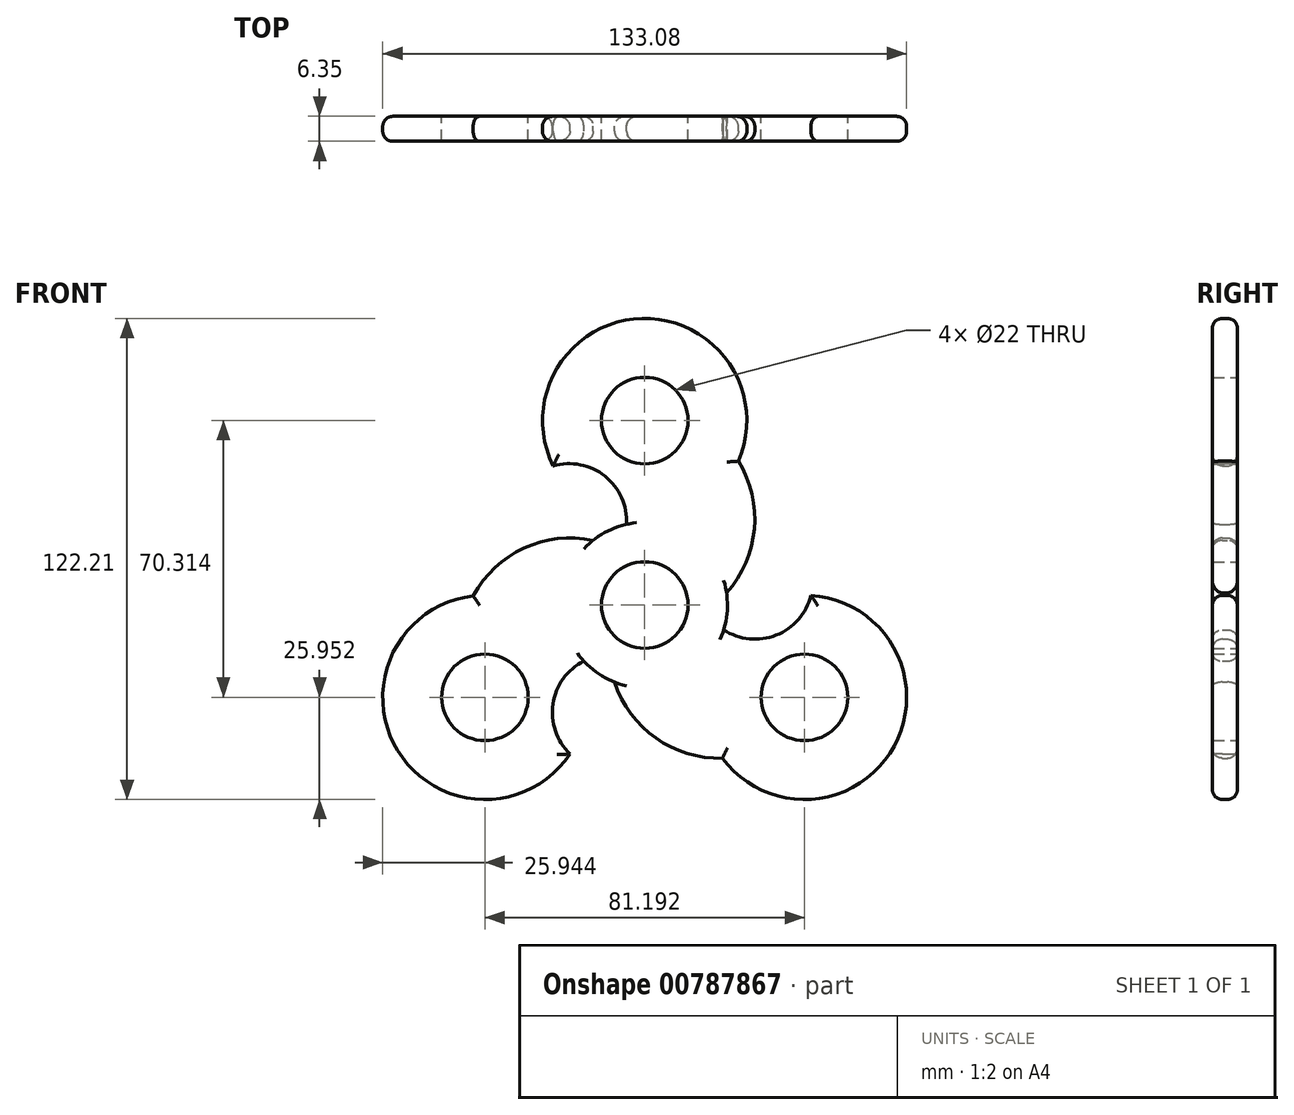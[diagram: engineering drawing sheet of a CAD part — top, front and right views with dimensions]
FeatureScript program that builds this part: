
annotation { "Feature Type Name" : "Feature", "Feature Type Description" : "" }
export const myFeature = defineFeature(function(context is Context, id is Id, definition is map)
    precondition{}
    {
        {
            var Q0;
            Q0=qCreatedBy(makeId("Front.planeOp"),FACE);
            var sketch = newSketch(context, id + "F0", { "sketchPlane" : qUnion([Q0])});
            skCircle(sketch, "E0", {"center": v(0, 0) * mm, "radius": 11 * mm});
            skCircle(sketch, "E1", {"center": v(0, 46.88) * mm, "radius": 11 * mm});
            skArc(sketch, "E2", {"start": v(-15.47, -14.24) * mm, "mid": v(-11.88, -17.34) * mm, "end": v(-7.69, -19.56) * mm});
            skArc(sketch, "E3", {"start": v(20.79, 3.12) * mm, "mid": v(27.85, 19.34) * mm, "end": v(23.81, 36.56) * mm});
            skArc(sketch, "E4", {"start": v(-4.6, 20.51) * mm, "mid": v(-10.08, 32.75) * mm, "end": v(-23.24, 35.33) * mm});
            skArc(sketch, "E5.trimOffspring", {"start": v(23.81, 36.56) * mm, "mid": v(-0.68, 72.82) * mm, "end": v(-23.24, 35.33) * mm});
            skCircle(sketch, "E6.1.0", {"center": v(-40.6, -23.44) * mm, "radius": 11 * mm});
            skArc(sketch, "E6.1.1", {"start": v(-13.1, 16.44) * mm, "mid": v(-30.67, 14.45) * mm, "end": v(-43.57, 2.34) * mm});
            skArc(sketch, "E6.1.2", {"start": v(-43.57, 2.34) * mm, "mid": v(-62.72, -37) * mm, "end": v(-18.98, -37.8) * mm});
            skArc(sketch, "E6.1.3", {"start": v(-15.47, -14.24) * mm, "mid": v(-23.32, -25.1) * mm, "end": v(-18.98, -37.8) * mm});
            skArc(sketch, "E6.1.4", {"start": v(20.06, -6.28) * mm, "mid": v(20.96, -1.62) * mm, "end": v(20.79, 3.12) * mm});
            skCircle(sketch, "E6.2.0", {"center": v(40.6, -23.44) * mm, "radius": 11 * mm});
            skArc(sketch, "E6.2.1", {"start": v(-7.69, -19.56) * mm, "mid": v(2.82, -33.79) * mm, "end": v(19.76, -38.9) * mm});
            skArc(sketch, "E6.2.2", {"start": v(19.76, -38.9) * mm, "mid": v(63.4, -35.82) * mm, "end": v(42.22, 2.46) * mm});
            skArc(sketch, "E6.2.3", {"start": v(20.06, -6.28) * mm, "mid": v(33.4, -7.64) * mm, "end": v(42.22, 2.46) * mm});
            skArc(sketch, "E6.2.4", {"start": v(-4.6, 20.51) * mm, "mid": v(-9.08, 18.96) * mm, "end": v(-13.1, 16.44) * mm});
            skPoint(sketch, "E7.orphan", {"position": v(-19.9, 6.76) * mm});
            skPoint(sketch, "E8.orphan", {"position": v(4.1, -20.62) * mm});
            skPoint(sketch, "E9.orphan", {"position": v(15.8, 13.86) * mm});
            skSolve(sketch);
        }
        {
            var Q0;
            Q0 = qSketchRegion(id + "F0", true);
            extrude(context, id + "F1", {"entities" : qUnion([Q0]), "depth" : 6.35 * mm, "offsetDistance" : 25.4 * mm});
        }
        {
            var Q0;
            Q0=makeQuery(id+"F1.opExtrude","CAP_EDGE",EDGE,{"disambiguationData":[OSD([sQuery(id+"F0.wireOp",EDGE,"E5.trimOffspring")])],"isStart":false});
            var Q1;
            Q1=makeQuery(id+"F1.opExtrude","CAP_EDGE",EDGE,{"disambiguationData":[OSD([sQuery(id+"F0.wireOp",EDGE,"E3")])],"isStart":false});
            var Q2;
            Q2=makeQuery(id+"F1.opExtrude","CAP_EDGE",EDGE,{"disambiguationData":[OSD([sQuery(id+"F0.wireOp",EDGE,"E4")])],"isStart":false});
            var Q3;
            Q3=makeQuery(id+"F1.opExtrude","CAP_EDGE",EDGE,{"disambiguationData":[OSD([sQuery(id+"F0.wireOp",EDGE,"E6.1.4")])],"isStart":false});
            var Q4;
            Q4=makeQuery(id+"F1.opExtrude","CAP_EDGE",EDGE,{"disambiguationData":[OSD([sQuery(id+"F0.wireOp",EDGE,"E6.2.3")])],"isStart":false});
            var Q5;
            Q5=makeQuery(id+"F1.opExtrude","CAP_EDGE",EDGE,{"disambiguationData":[OSD([sQuery(id+"F0.wireOp",EDGE,"E6.2.2")])],"isStart":false});
            var Q6;
            Q6=makeQuery(id+"F1.opExtrude","CAP_EDGE",EDGE,{"disambiguationData":[OSD([sQuery(id+"F0.wireOp",EDGE,"E6.2.1")])],"isStart":false});
            var Q7;
            Q7=makeQuery(id+"F1.opExtrude","CAP_EDGE",EDGE,{"disambiguationData":[OSD([sQuery(id+"F0.wireOp",EDGE,"E2")])],"isStart":false});
            var Q8;
            Q8=makeQuery(id+"F1.opExtrude","CAP_EDGE",EDGE,{"disambiguationData":[OSD([sQuery(id+"F0.wireOp",EDGE,"E6.1.3")])],"isStart":false});
            var Q9;
            Q9=makeQuery(id+"F1.opExtrude","CAP_EDGE",EDGE,{"disambiguationData":[OSD([sQuery(id+"F0.wireOp",EDGE,"E6.1.2")])],"isStart":false});
            var Q10;
            Q10=makeQuery(id+"F1.opExtrude","CAP_EDGE",EDGE,{"disambiguationData":[OSD([sQuery(id+"F0.wireOp",EDGE,"E6.1.1")])],"isStart":false});
            var Q11;
            Q11=makeQuery(id+"F1.opExtrude","CAP_EDGE",EDGE,{"disambiguationData":[OSD([sQuery(id+"F0.wireOp",EDGE,"E6.2.4")])],"isStart":false});
            var Q12;
            Q12=makeQuery(id+"F1.opExtrude","CAP_EDGE",EDGE,{"disambiguationData":[OSD([sQuery(id+"F0.wireOp",EDGE,"E5.trimOffspring")])],"isStart":true});
            var Q13;
            Q13=makeQuery(id+"F1.opExtrude","CAP_EDGE",EDGE,{"disambiguationData":[OSD([sQuery(id+"F0.wireOp",EDGE,"E3")])],"isStart":true});
            var Q14;
            Q14=makeQuery(id+"F1.opExtrude","CAP_EDGE",EDGE,{"disambiguationData":[OSD([sQuery(id+"F0.wireOp",EDGE,"E4")])],"isStart":true});
            var Q15;
            Q15=makeQuery(id+"F1.opExtrude","CAP_EDGE",EDGE,{"disambiguationData":[OSD([sQuery(id+"F0.wireOp",EDGE,"E6.1.1")])],"isStart":true});
            var Q16;
            Q16=makeQuery(id+"F1.opExtrude","CAP_EDGE",EDGE,{"disambiguationData":[OSD([sQuery(id+"F0.wireOp",EDGE,"E6.2.4")])],"isStart":true});
            var Q17;
            Q17=makeQuery(id+"F1.opExtrude","CAP_EDGE",EDGE,{"disambiguationData":[OSD([sQuery(id+"F0.wireOp",EDGE,"E6.1.2")])],"isStart":true});
            var Q18;
            Q18=makeQuery(id+"F1.opExtrude","CAP_EDGE",EDGE,{"disambiguationData":[OSD([sQuery(id+"F0.wireOp",EDGE,"E6.1.3")])],"isStart":true});
            var Q19;
            Q19=makeQuery(id+"F1.opExtrude","CAP_EDGE",EDGE,{"disambiguationData":[OSD([sQuery(id+"F0.wireOp",EDGE,"E2")])],"isStart":true});
            var Q20;
            Q20=makeQuery(id+"F1.opExtrude","CAP_EDGE",EDGE,{"disambiguationData":[OSD([sQuery(id+"F0.wireOp",EDGE,"E6.2.1")])],"isStart":true});
            var Q21;
            Q21=makeQuery(id+"F1.opExtrude","CAP_EDGE",EDGE,{"disambiguationData":[OSD([sQuery(id+"F0.wireOp",EDGE,"E6.2.2")])],"isStart":true});
            var Q22;
            Q22=makeQuery(id+"F1.opExtrude","CAP_EDGE",EDGE,{"disambiguationData":[OSD([sQuery(id+"F0.wireOp",EDGE,"E6.2.3")])],"isStart":true});
            var Q23;
            Q23=makeQuery(id+"F1.opExtrude","CAP_EDGE",EDGE,{"disambiguationData":[OSD([sQuery(id+"F0.wireOp",EDGE,"E6.1.4")])],"isStart":true});
            fillet(context, id + "F2", {"entities" : qUnion([Q0, Q1, Q2, Q3, Q4, Q5, Q6, Q7, Q8, Q9, Q10, Q11, Q12, Q13, Q14, Q15, Q16, Q17, Q18, Q19, Q20, Q21, Q22, Q23]), "radius" : 2.54 * mm, "tangentPropagation" : true, "allowEdgeOverflow" : false});
        }
    });
